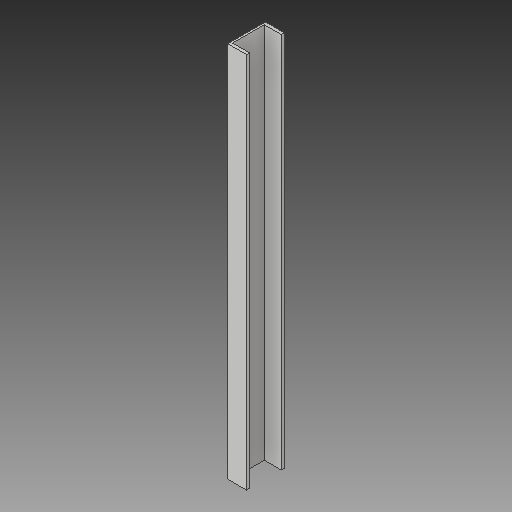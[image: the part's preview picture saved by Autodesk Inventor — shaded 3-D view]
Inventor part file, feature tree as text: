
AUTODESK INVENTOR PART (.ipt)
format: ipt  version: 2019 (Build 230136000, 136)  size: 90,112 bytes
history: native  units: in
note: dims shown in document units (in); Inventor stores cm internally (conversion verified against a paired STEP export)
features: other x3, sketch x1
ambient origin geometry x8: Origin, YZ Plane, XZ Plane, XY Plane, X Axis, Y Axis, Z Axis, Center Point
bodies: Solid1 (feature_tree)
feature tree (4):
  other  "Channel1_MIR.ipt"
  other  "Solid1::Channel1_MIR.ipt"
  other  "TaggingFeature1"
  sketch  "Sketch1"  dims[d0=0.3937in]
